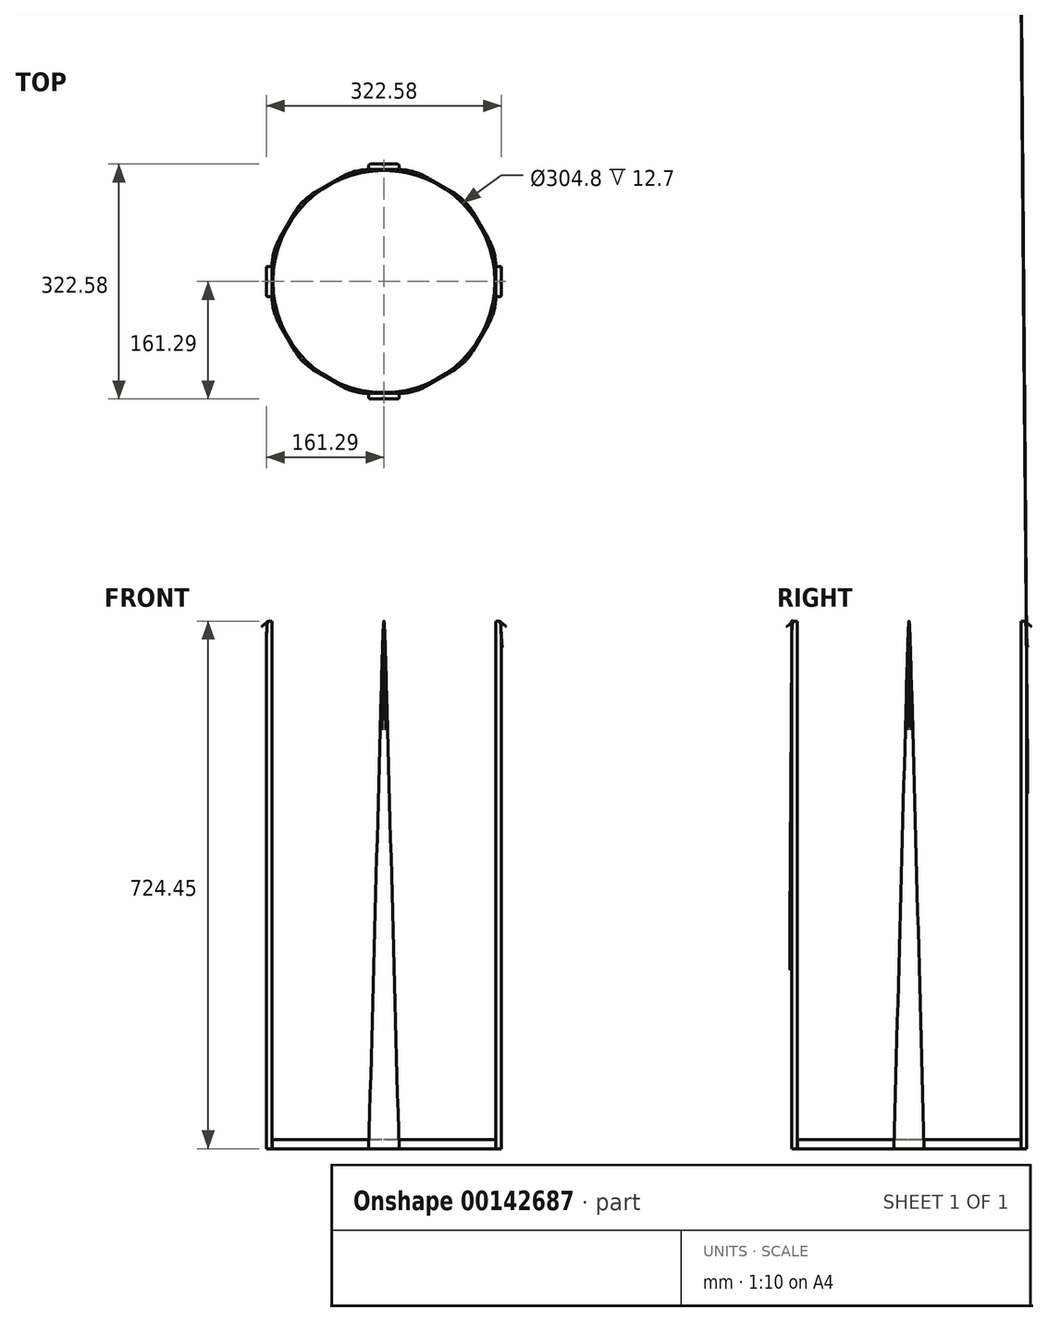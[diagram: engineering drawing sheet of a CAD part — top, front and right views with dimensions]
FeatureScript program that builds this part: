
annotation { "Feature Type Name" : "Feature", "Feature Type Description" : "" }
export const myFeature = defineFeature(function(context is Context, id is Id, definition is map)
    precondition{}
    {
        {
            var Q0;
            Q0=qCreatedBy(makeId("Top.planeOp"),FACE);
            var sketch = newSketch(context, id + "F0", { "sketchPlane" : qUnion([Q0])});
            skCircle(sketch, "E0.cCircle", {"center": v(0, 0) * mm, "radius": 153.67 * mm, "construction": true});
            skLineSegment(sketch, "E0.0", {"start": v(-112.5, -112.5) * mm, "end": v(-153.67, -41.18) * mm});
            skLineSegment(sketch, "E0.1", {"start": v(-153.67, -41.18) * mm, "end": v(-153.67, 41.18) * mm});
            skLineSegment(sketch, "E0.2", {"start": v(-153.67, 41.18) * mm, "end": v(-112.5, 112.5) * mm});
            skLineSegment(sketch, "E0.3", {"start": v(-112.5, 112.5) * mm, "end": v(-41.18, 153.67) * mm});
            skLineSegment(sketch, "E0.4", {"start": v(-41.18, 153.67) * mm, "end": v(41.18, 153.67) * mm});
            skLineSegment(sketch, "E0.5", {"start": v(41.18, 153.67) * mm, "end": v(112.5, 112.5) * mm});
            skLineSegment(sketch, "E0.6", {"start": v(112.5, 112.5) * mm, "end": v(153.67, 41.18) * mm});
            skLineSegment(sketch, "E0.7", {"start": v(153.67, 41.18) * mm, "end": v(153.67, -41.18) * mm});
            skLineSegment(sketch, "E0.8", {"start": v(153.67, -41.18) * mm, "end": v(112.5, -112.5) * mm});
            skLineSegment(sketch, "E0.9", {"start": v(112.5, -112.5) * mm, "end": v(41.18, -153.67) * mm});
            skLineSegment(sketch, "E0.10", {"start": v(41.18, -153.67) * mm, "end": v(-41.18, -153.67) * mm});
            skLineSegment(sketch, "E0.11", {"start": v(-41.18, -153.67) * mm, "end": v(-112.5, -112.5) * mm});
            skPoint(sketch, "E0.0.midPoint", {"position": v(-133.08, -76.83) * mm});
            skCircle(sketch, "E1", {"center": v(0, 0) * mm, "radius": 152.4 * mm});
            skSolve(sketch);
        }
        {
            var Q0;
            Q0 = qSketchRegion(id + "F0", true);
            extrude(context, id + "F1", {"entities" : qUnion([Q0]), "depth" : 12.7 * mm});
        }
        {
            var Q0;
            Q0=makeQuery(id+"F1.opExtrude","SWEPT_EDGE",EDGE,{"disambiguationData":[OSD([sQuery(id+"F0.wireOp",EDGE,"E0.10"),sQuery(id+"F0.wireOp",EDGE,"E0.11")])]});
            var Q1;
            Q1=makeQuery(id+"F1.opExtrude","SWEPT_EDGE",EDGE,{"disambiguationData":[OSD([sQuery(id+"F0.wireOp",EDGE,"E0.9"),sQuery(id+"F0.wireOp",EDGE,"E0.10")])]});
            var Q2;
            Q2=makeQuery(id+"F1.opExtrude","SWEPT_EDGE",EDGE,{"disambiguationData":[OSD([sQuery(id+"F0.wireOp",EDGE,"E0.8"),sQuery(id+"F0.wireOp",EDGE,"E0.9")])]});
            var Q3;
            Q3=makeQuery(id+"F1.opExtrude","SWEPT_EDGE",EDGE,{"disambiguationData":[OSD([sQuery(id+"F0.wireOp",EDGE,"E0.7"),sQuery(id+"F0.wireOp",EDGE,"E0.8")])]});
            var Q4;
            Q4=makeQuery(id+"F1.opExtrude","SWEPT_EDGE",EDGE,{"disambiguationData":[OSD([sQuery(id+"F0.wireOp",EDGE,"E0.6"),sQuery(id+"F0.wireOp",EDGE,"E0.7")])]});
            var Q5;
            Q5=makeQuery(id+"F1.opExtrude","SWEPT_EDGE",EDGE,{"disambiguationData":[OSD([sQuery(id+"F0.wireOp",EDGE,"E0.5"),sQuery(id+"F0.wireOp",EDGE,"E0.6")])]});
            var Q6;
            Q6=makeQuery(id+"F1.opExtrude","SWEPT_EDGE",EDGE,{"disambiguationData":[OSD([sQuery(id+"F0.wireOp",EDGE,"E0.4"),sQuery(id+"F0.wireOp",EDGE,"E0.5")])]});
            var Q7;
            Q7=makeQuery(id+"F1.opExtrude","SWEPT_EDGE",EDGE,{"disambiguationData":[OSD([sQuery(id+"F0.wireOp",EDGE,"E0.3"),sQuery(id+"F0.wireOp",EDGE,"E0.4")])]});
            var Q8;
            Q8=makeQuery(id+"F1.opExtrude","SWEPT_EDGE",EDGE,{"disambiguationData":[OSD([sQuery(id+"F0.wireOp",EDGE,"E0.2"),sQuery(id+"F0.wireOp",EDGE,"E0.3")])]});
            var Q9;
            Q9=makeQuery(id+"F1.opExtrude","SWEPT_EDGE",EDGE,{"disambiguationData":[OSD([sQuery(id+"F0.wireOp",EDGE,"E0.1"),sQuery(id+"F0.wireOp",EDGE,"E0.2")])]});
            var Q10;
            Q10=makeQuery(id+"F1.opExtrude","SWEPT_EDGE",EDGE,{"disambiguationData":[OSD([sQuery(id+"F0.wireOp",EDGE,"E0.0"),sQuery(id+"F0.wireOp",EDGE,"E0.1")])]});
            var Q11;
            Q11=makeQuery(id+"F1.opExtrude","SWEPT_EDGE",EDGE,{"disambiguationData":[OSD([sQuery(id+"F0.wireOp",EDGE,"E0.0"),sQuery(id+"F0.wireOp",EDGE,"E0.11")])]});
            fillet(context, id + "F2", {"entities" : qUnion([Q0, Q1, Q2, Q3, Q4, Q5, Q6, Q7, Q8, Q9, Q10, Q11]), "radius" : 76.2 * mm, "tangentPropagation" : true, "allowEdgeOverflow" : false});
        }
        {
            var Q0;
            Q0=makeQuery(id+"F1.opExtrude","SWEPT_FACE",FACE,{"disambiguationData":[OSD([sQuery(id+"F0.wireOp",EDGE,"E0.7")])]});
            var sketch = newSketch(context, id + "F3", { "sketchPlane" : qUnion([Q0])});
            skLineSegment(sketch, "E2", {"start": v(-20.76, 0) * mm, "end": v(0, 761.72) * mm});
            skLineSegment(sketch, "E3", {"start": v(0, 761.72) * mm, "end": v(20.76, 0) * mm});
            skSolve(sketch);
        }
        {
            var Q0;
            {var subQ1=sQuery(id+"F0.wireOp",EDGE,"E0.7");var subQ2=makeQuery(id+"F1.opExtrude","CAP_EDGE",EDGE,{"disambiguationData":[OSD([subQ1])],"isStart":true});Q0=makeQuery(id+"F3.imprint","IMPRINT",FACE,{"disambiguationData":[TD([[makeQuery(id+"F3.imprint","IMPRINT",EDGE,{"derivedFrom":subQ2}),-1.0]])]});}
            var Q1;
            {var subQ0=sQuery(id+"F3.wireOp",EDGE,"E3");var subQ1=sQuery(id+"F3.wireOp",EDGE,"E2");var subQ2=makeQuery(id+"F3.imprint","INTERSECT",VERTEX,{"derivedFrom":[subQ1,subQ0]});Q1=makeQuery(id+"F3.imprint","IMPRINT",FACE,{"disambiguationData":[TD([[makeQuery(id+"F3.imprint","IMPRINT",EDGE,{"disambiguationData":[TD([[subQ2,1.0]])],"derivedFrom":subQ1}),-1.0]])]});}
            extrude(context, id + "F4", {"entities" : qUnion([Q0, Q1]), "depth" : 7.62 * mm});
        }
        {
            var Q0;
            Q0=makeQuery(id+"F4.opExtrude","SWEPT_EDGE",EDGE,{"disambiguationData":[OSD([sQuery(id+"F3.wireOp",EDGE,"E2"),sQuery(id+"F3.wireOp",EDGE,"E3")])]});
            fillet(context, id + "F5", {"entities" : qUnion([Q0]), "radius" : 5.08 * mm, "tangentPropagation" : true, "rho" : 0.8, "crossSection" : FilletCrossSection.CONIC, "allowEdgeOverflow" : false});
        }
        {
            var Q0;
            Q0=makeQuery(id+"F4.opExtrude","CAP_EDGE",EDGE,{"disambiguationData":[OSD([sQuery(id+"F3.wireOp",EDGE,"E2")])],"isStart":false});
            fillet(context, id + "F6", {"entities" : qUnion([Q0]), "radius" : 2.54 * mm, "tangentPropagation" : true, "rho" : 0.5, "crossSection" : FilletCrossSection.CONIC, "allowEdgeOverflow" : false});
        }
        {
            var Q0;
            Q0=makeQuery(id+"F4.opExtrude","SWEPT_BODY",BODY,{"disambiguationData":[OSD([sQuery(id+"F0.wireOp",EDGE,"E0.7"),sQuery(id+"F3.wireOp",EDGE,"E2"),sQuery(id+"F3.wireOp",EDGE,"E3")])]});
            var Q1;
            Q1=makeQuery(id+"F1.opExtrude","CAP_EDGE",EDGE,{"disambiguationData":[OSD([sQuery(id+"F0.wireOp",EDGE,"E1")])],"isStart":false});
            circularPattern(context, id + "F7", {"entities" : qUnion([Q0]), "axis" : qUnion([Q1]), "angle" : 90 * degree, "instanceCount" : 4});
        }
    });
